# Revit family: ДВО-01 40 Вт 595
name_source: partatom
category: Осветительные приборы
units: mm (PartAtom-declared; Revit-internal decimal feet)

## family parameters
Всегда вертикально = Да
Заголовок OmniClass = Luminaries for Internal Lighting
Источник света = Да
Номер OmniClass = 23.80.70.11
Общий = Нет
Основа = Потолок
При загрузке вырезать с полостями = Нет
Размер круглого соединителя = Использовать диаметр
Тип детали = Нормальный
Точка расчета площади = Нет

## types (12) — shared parameters
ADSK_Размер_Высота = 45 мм
ADSK_Размер_Длина = 595 мм
ADSK_Размер_Ширина = 595 мм
URL = http://innolux.pro
Блок аварийного питания = нет
Бренд светодиодов = EDISON
Вес светильника = 2.9 кг
Гарантия = 7 лет
Диапазон рабочих температур = - 20 + 40°C
Диммирование = нет
Изготовитель = INNOLUX
Индекс цветопередачи = >80
Класс защиты от поражения током = I
Класс светораспределения по ГОСТ 54350-2011 = П
Климатическое исполнение = УХЛ 4
Кол-во светодиодов = 72
Количество в упаковке = 4
Количество модулей = 4
Коэффициент мощности = >0.95
>0.95
>0.95
Коэффициент пульсации = <5%
Материал корпуса = Металл, окрашенный, белый, матовый
Материал рассеивателя = Полистирол
Напряжение = 176-264 В
Объём упаковки = 0.22*0.61*0.61 м
Полная установленная мощность = 40 В·А
Потребляемый ток = 0
Светофильтр = 16777215
Сила тока = 0.18 А
Смещение цветовой температуры при затухании лампы = <Нет>
Способ монтажа = Встраиваемый / Накладной
Срок службы = 80000
Степень защиты (IP) = 40
Тип кривой силы света по ГОСТ 54350-2011 = Д
Типоразмер светодиода = 2835
Угол наклона = 90.00°
Цвет корпуса = Белый
Частота сети = 50 / 60 Гц

## per-type parameters (varying)
| type | Артикул | Время импульса пускового тока | Габаритная яркость | Категория по ограничению яркости | Пусковой ток | Световой поток модуля | Тип рассеивателя | Файл фотометрической сетки | Эффективность светильника |
| ДВО-01-П-40-3К-IP40-Армстронг | 14772 | 200 мс |  | 3 | 26 А | 1277 | призма | INNOLUX 14 772 DVO-01-P-40-3K-IP40.ies | 119 |
| ДВО-01-П-40-4К-IP40-Армстронг | 14775 | 200 мс |  | 3 | 26 А | 1277 | призма | INNOLUX 14 772 DVO-01-P-40-3K-IP40.ies | 119 |
| ДВО-01-П-40-5К-IP40-Армстронг | 14778 | 200 мс |  | 3 | 26 А | 1277 | призма | INNOLUX 14 778 DVO-01-P-40-5K-IP40.ies | 119 |
| ДВО-01-О-40-3К-IP40-Армстронг | 14781 | 200 мс | <5000 кд / м2 | 1 | 26 А | 1406 | опал | INNOLUX 14 781 DVO-01-O-40-3K-IP40.ies | 105 |
| ДВО-01-О-40-4К-IP40-Армстронг | 14784 | 200 мс | <5000 кд / м2 | 1 | 26 А | 1406 | опал | INNOLUX 14 784 DVO-01-O-40-4K-IP40.ies | 105 |
| ДВО-01-О-40-5К-IP40-Армстронг | 14787 | 200 мс | <5000 кд / м2 | 1 | 26 А | 1406 | опал | INNOLUX 14 787 DVO-01-O-40-5K-IP40.ies | 105 |
| ДВО-01-К-40-3К-IP40-Армстронг | 82674 | 2.8 мс | <5000 кд / м2 | 1 | 20.4 А | 1344 | колотый лёд | INNOLUX 82 674 DVO-01-K-40-3K-IP40.ies | 125 |
| ДВО-01-К-40-4К-IP40-Армстронг | 82677 | 2.8 мс | <5000 кд / м2 | 1 | 20.4 А | 1344 | колотый лёд | INNOLUX 82 677 DVO-01-K-40-4K-IP40.ies | 125 |
| ДВО-01-К-40-5К-IP40-Армстронг | 82680 | 2.8 мс | <5000 кд / м2 | 1 | 20.4 А | 1344 | колотый лёд | INNOLUX 82 680 DVO-01-K-40-5K-IP40.ies | 125 |
| ДВО-01-МП-40-3К-IP40-Армстронг | 80115 | 2.8 мс | <5000 кд / м2 | 1 | 20.4 А | 1263 | микропризма | INNOLUX 80 115 DVO-01-MP-40-3K-IP40.ies | 118 |
| ДВО-01-МП-40-4К-IP40-Армстронг | 80118 | 2.8 мс | <5000 кд / м2 | 1 | 20.4 А | 1263 | микропризма | INNOLUX 80 118 DVO-01-MP-40-4K-IP40.ies | 118 |
| ДВО-01-МП-40-5К-IP40-Армстронг | 80121 | 2.8 мс | <5000 кд / м2 | 1 | 20.4 А | 1263 | микропризма | INNOLUX 80 121 DVO-01-MP-40-5K-IP40.ies | 118 |
